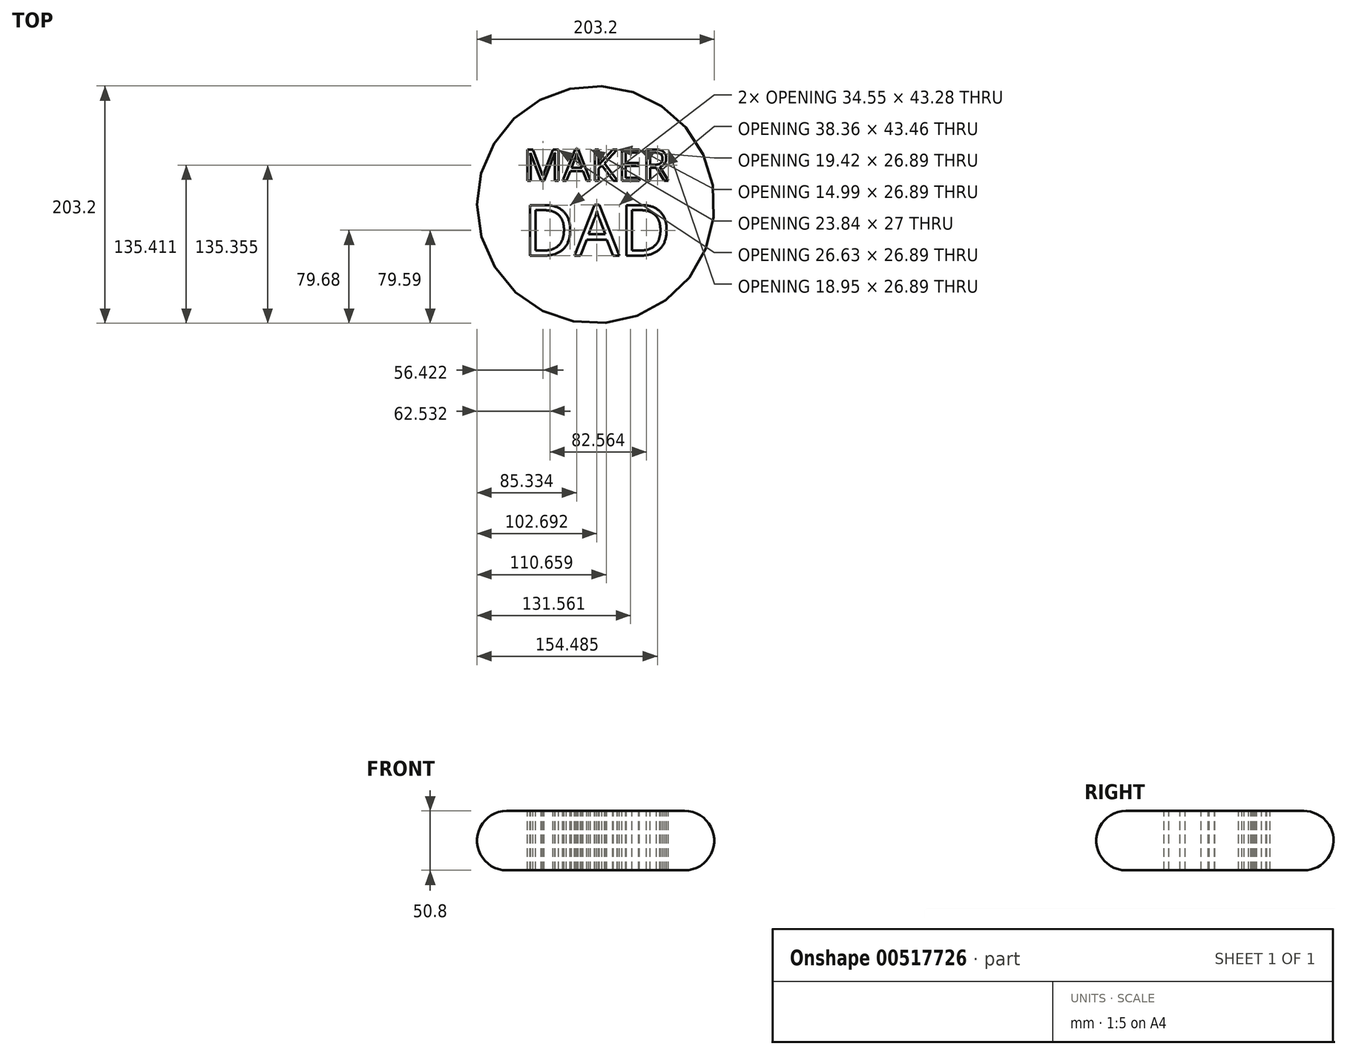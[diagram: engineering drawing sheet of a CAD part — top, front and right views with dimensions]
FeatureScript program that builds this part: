
annotation { "Feature Type Name" : "Feature", "Feature Type Description" : "" }
export const myFeature = defineFeature(function(context is Context, id is Id, definition is map)
    precondition{}
    {
        {
            var Q0;
            Q0=qCreatedBy(makeId("Front.planeOp"),FACE);
            var sketch = newSketch(context, id + "F0", { "sketchPlane" : qUnion([Q0])});
            skArc(sketch, "E0", {"start": v(-34.71, 39.45) * mm, "mid": v(-60.11, 14.05) * mm, "end": v(-34.71, -11.35) * mm});
            skLineSegment(sketch, "E1", {"start": v(-34.71, -11.35) * mm, "end": v(41.49, -11.35) * mm});
            skLineSegment(sketch, "E2", {"start": v(41.49, -11.35) * mm, "end": v(41.49, 39.45) * mm});
            skLineSegment(sketch, "E3", {"start": v(-34.71, 39.45) * mm, "end": v(41.49, 39.45) * mm});
            skSolve(sketch);
        }
        {
            var Q0;
            Q0 = qSketchRegion(id + "F0", true);
            var Q1;
            Q1=sQuery(id+"F0.wireOp",EDGE,"E2");
            revolve(context, id + "F1", {"entities" : qUnion([Q0]), "axis" : qUnion([Q1]), "revolveType" : RevolveType.FULL});
        }
        {
            var Q0;
            Q0=qCreatedBy(makeId("Top.planeOp"),FACE);
            var sketch = newSketch(context, id + "F2", { "sketchPlane" : qUnion([Q0])});
            skText(sketch, "E4", { "text": "MAKER", "fontName": "OpenSans-Regular.ttf"});
            skText(sketch, "E5", { "text": "DAD", "fontName": "OpenSans-Regular.ttf"});
            const initialGuessF2  = {"E4": [-0.0207, 0.02031, 1, 0, 0.02712], "E5": [-0.0208, -0.04365, 1, 0, 0.04365]};
            skSetInitialGuess(sketch, initialGuessF2);
            skSolve(sketch);
        }
        {
            var Q0;
            Q0 = qSketchRegion(id + "F2", true);
            extrude(context, id + "F3", {"entities" : qUnion([Q0]), "operationType" : NewBodyOperationType.REMOVE, "endBound" : BoundingType.SYMMETRIC, "oppositeDirection" : true, "depth" : 381 * mm, "offsetDistance" : 25.4 * mm});
        }
    });
